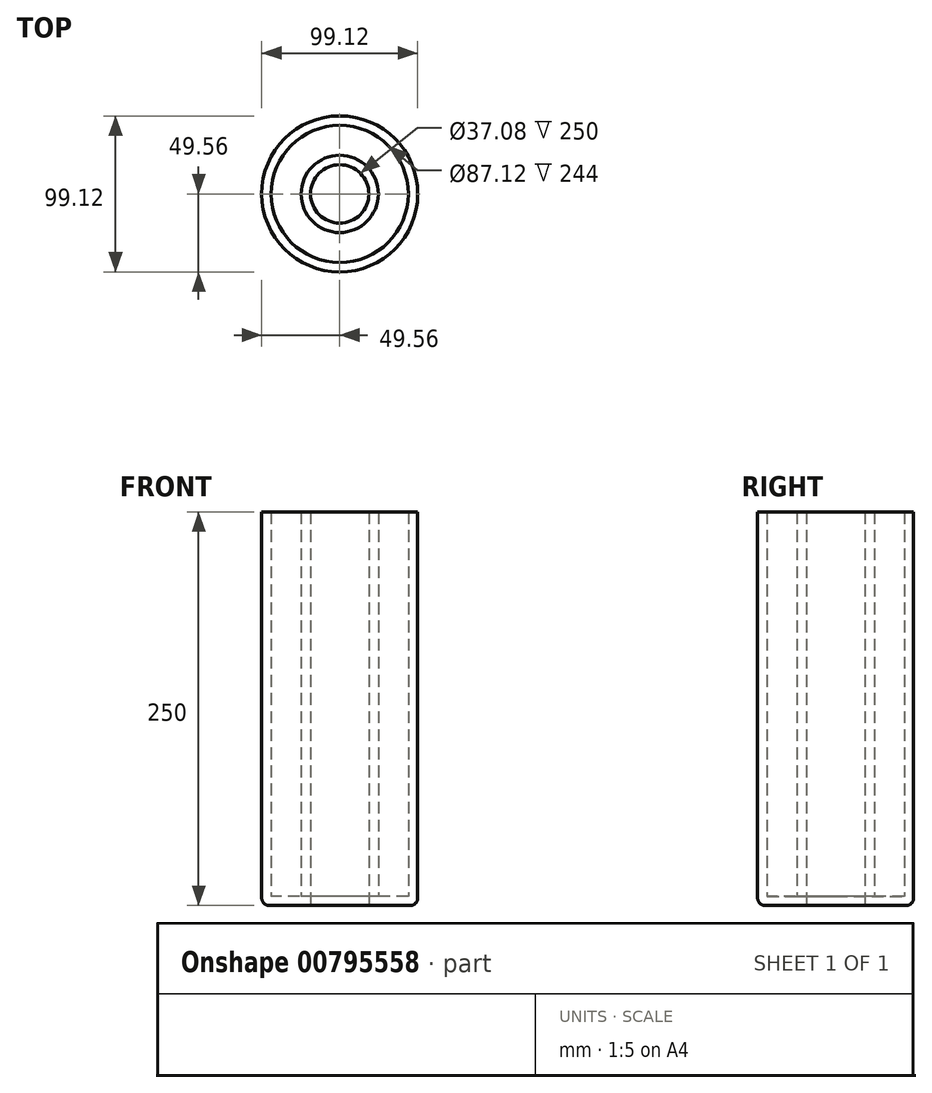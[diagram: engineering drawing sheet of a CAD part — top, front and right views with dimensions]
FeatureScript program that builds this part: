
annotation { "Feature Type Name" : "Feature", "Feature Type Description" : "" }
export const myFeature = defineFeature(function(context is Context, id is Id, definition is map)
    precondition{}
    {
        {
            var Q0;
            Q0=qCreatedBy(makeId("Top.planeOp"),FACE);
            var sketch = newSketch(context, id + "F0", { "sketchPlane" : qUnion([Q0])});
            skCircle(sketch, "E0", {"center": v(0, 0) * mm, "radius": 49.56 * mm});
            skCircle(sketch, "E1", {"center": v(0, 0) * mm, "radius": 18.54 * mm});
            skSolve(sketch);
        }
        {
            var Q0;
            Q0=makeQuery(id+"F0.imprint","IMPRINT",FACE,{"disambiguationData":[TD([[makeQuery(id+"F0.imprint","IMPRINT",EDGE,{"derivedFrom":sQuery(id+"F0.wireOp",EDGE,"E0")}),1.0]])]});
            extrude(context, id + "F1", {"entities" : qUnion([Q0]), "depth" : 250 * mm, "offsetDistance" : 25.4 * mm});
        }
        {
            var Q0;
            Q0=makeQuery(id+"F1.opExtrude","CAP_EDGE",EDGE,{"disambiguationData":[OSD([sQuery(id+"F0.wireOp",EDGE,"E0")])],"isStart":true});
            fillet(context, id + "F2", {"entities" : qUnion([Q0]), "radius" : 5 * mm, "tangentPropagation" : true, "allowEdgeOverflow" : false});
        }
        {
            var Q0;
            Q0=makeQuery(id+"F1.opExtrude","CAP_FACE",FACE,{"disambiguationData":[OSD([sQuery(id+"F0.wireOp",EDGE,"E0"),sQuery(id+"F0.wireOp",EDGE,"E1")])],"isStart":false});
            shell(context, id + "F3", {"entities" : qUnion([Q0]), "thickness" : 6 * mm});
        }
    });
